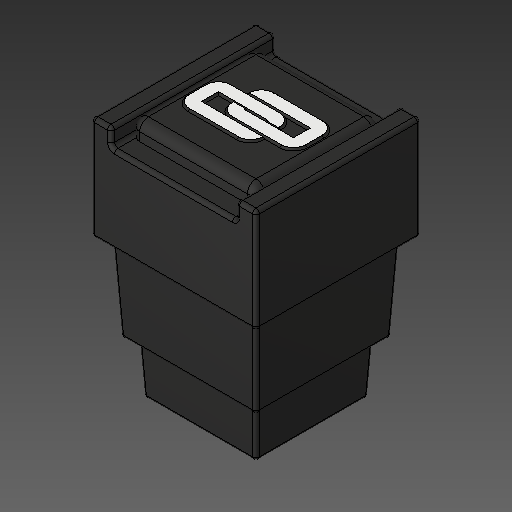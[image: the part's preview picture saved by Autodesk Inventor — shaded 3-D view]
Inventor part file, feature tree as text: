
AUTODESK INVENTOR PART (.ipt)
format: ipt  version: 2018.2 (Build 222227000, 227)  size: 250,368 bytes
history: native  units: mm
features: other x2, fillet x2
ambient origin geometry x8: Origin, YZ Plane, XZ Plane, XY Plane, X Axis, Y Axis, Z Axis, Center Point
bodies: Body1 (feature_tree), Body2 (feature_tree)
feature tree (4):
  other  "ソリッド1"
  other  "ソリッド2"
  fillet  "Fillet1"  [1 undecoded]
  fillet  "Fillet3"  [1 undecoded]
note: 2 required parameter values undecoded (feature->parameter linkage not recoverable at this tier; creation-order binding heuristic only, values carry confidence <= 0.55)
